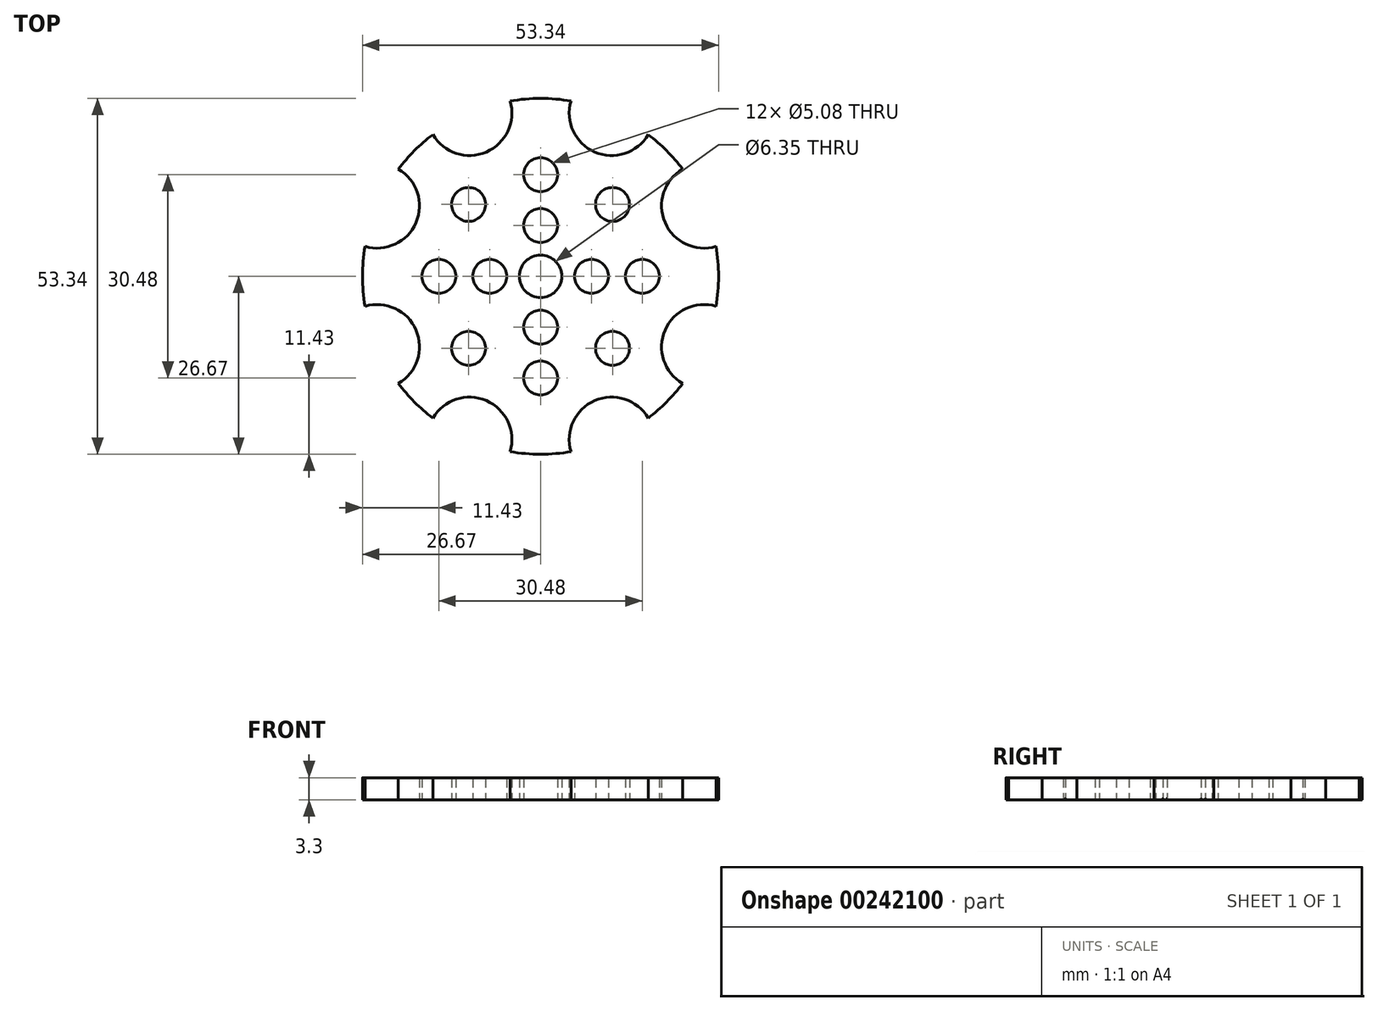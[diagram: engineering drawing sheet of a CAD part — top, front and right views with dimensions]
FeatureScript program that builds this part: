
annotation { "Feature Type Name" : "Feature", "Feature Type Description" : "" }
export const myFeature = defineFeature(function(context is Context, id is Id, definition is map)
    precondition{}
    {
        {
            var Q0;
            Q0=qCreatedBy(makeId("Top.planeOp"),FACE);
            var sketch = newSketch(context, id + "F0", { "sketchPlane" : qUnion([Q0])});
            skCircle(sketch, "E0", {"center": v(0, 0) * mm, "radius": 26.67 * mm});
            skCircle(sketch, "E1", {"center": v(0, 7.62) * mm, "radius": 2.54 * mm});
            skCircle(sketch, "E2", {"center": v(0, 15.24) * mm, "radius": 2.54 * mm});
            skCircle(sketch, "E3", {"center": v(7.62, 0) * mm, "radius": 2.54 * mm});
            skCircle(sketch, "E4", {"center": v(15.24, 0) * mm, "radius": 2.54 * mm});
            skCircle(sketch, "E5.MirrorC", {"center": v(-10.78, -10.78) * mm, "radius": 2.54 * mm});
            skCircle(sketch, "E6.MirrorC", {"center": v(10.78, 10.78) * mm, "radius": 2.54 * mm});
            skCircle(sketch, "E7", {"center": v(-24.48, 10.57) * mm, "radius": 6.35 * mm});
            skCircle(sketch, "E8", {"center": v(-10.65, 24.45) * mm, "radius": 6.35 * mm});
            skCircle(sketch, "E9", {"center": v(0, 0) * mm, "radius": 3.18 * mm});
            skCircle(sketch, "E10.MirrorC", {"center": v(10.65, 24.45) * mm, "radius": 6.35 * mm});
            skCircle(sketch, "E11.MirrorC", {"center": v(24.48, 10.57) * mm, "radius": 6.35 * mm});
            skCircle(sketch, "E12.MirrorC", {"center": v(-24.48, -10.57) * mm, "radius": 6.35 * mm});
            skCircle(sketch, "E13.MirrorC", {"center": v(-10.65, -24.45) * mm, "radius": 6.35 * mm});
            skCircle(sketch, "E14.MirrorC", {"center": v(10.65, -24.45) * mm, "radius": 6.35 * mm});
            skCircle(sketch, "E15.MirrorC", {"center": v(24.48, -10.57) * mm, "radius": 6.35 * mm});
            skCircle(sketch, "E16.MirrorC", {"center": v(0, -7.62) * mm, "radius": 2.54 * mm});
            skCircle(sketch, "E17.MirrorC", {"center": v(0, -15.24) * mm, "radius": 2.54 * mm});
            skCircle(sketch, "E18.MirrorC", {"center": v(10.78, -10.78) * mm, "radius": 2.54 * mm});
            skCircle(sketch, "E19.MirrorC", {"center": v(-10.78, 10.78) * mm, "radius": 2.54 * mm});
            skCircle(sketch, "E20.MirrorC", {"center": v(-7.62, 0) * mm, "radius": 2.54 * mm});
            skCircle(sketch, "E21.MirrorC", {"center": v(-15.24, 0) * mm, "radius": 2.54 * mm});
            skSolve(sketch);
        }
        {
            var Q0;
            Q0=makeQuery(id+"F0.imprint","IMPRINT",FACE,{"disambiguationData":[TD([[makeQuery(id+"F0.imprint","IMPRINT",EDGE,{"derivedFrom":sQuery(id+"F0.wireOp",EDGE,"E1")}),-1.0]])]});
            extrude(context, id + "F1", {"entities" : qUnion([Q0]), "depth" : 3.3 * mm});
        }
        {
            var Q0;
            Q0=makeQuery(id+"F1.opExtrude","CAP_EDGE",EDGE,{"disambiguationData":[OSD([sQuery(id+"F0.wireOp",EDGE,"E21.MirrorC")])],"isStart":true});
            var Q1;
            Q1=makeQuery(id+"F1.opExtrude","CAP_EDGE",EDGE,{"disambiguationData":[OSD([sQuery(id+"F0.wireOp",EDGE,"E19.MirrorC")])],"isStart":true});
            var Q2;
            Q2=makeQuery(id+"F1.opExtrude","CAP_EDGE",EDGE,{"disambiguationData":[OSD([sQuery(id+"F0.wireOp",EDGE,"E20.MirrorC")])],"isStart":true});
            var Q3;
            Q3=makeQuery(id+"F1.opExtrude","CAP_EDGE",EDGE,{"disambiguationData":[OSD([sQuery(id+"F0.wireOp",EDGE,"E5.MirrorC")])],"isStart":true});
            var Q4;
            Q4=makeQuery(id+"F1.opExtrude","CAP_EDGE",EDGE,{"disambiguationData":[OSD([sQuery(id+"F0.wireOp",EDGE,"E16.MirrorC")])],"isStart":true});
            var Q5;
            Q5=makeQuery(id+"F1.opExtrude","CAP_EDGE",EDGE,{"disambiguationData":[OSD([sQuery(id+"F0.wireOp",EDGE,"E17.MirrorC")])],"isStart":true});
            var Q6;
            Q6=makeQuery(id+"F1.opExtrude","CAP_EDGE",EDGE,{"disambiguationData":[OSD([sQuery(id+"F0.wireOp",EDGE,"E18.MirrorC")])],"isStart":true});
            var Q7;
            Q7=makeQuery(id+"F1.opExtrude","CAP_EDGE",EDGE,{"disambiguationData":[OSD([sQuery(id+"F0.wireOp",EDGE,"E3")])],"isStart":true});
            var Q8;
            Q8=makeQuery(id+"F1.opExtrude","CAP_EDGE",EDGE,{"disambiguationData":[OSD([sQuery(id+"F0.wireOp",EDGE,"E1")])],"isStart":true});
            var Q9;
            Q9=makeQuery(id+"F1.opExtrude","CAP_EDGE",EDGE,{"disambiguationData":[OSD([sQuery(id+"F0.wireOp",EDGE,"E9")])],"isStart":true});
            var Q10;
            Q10=makeQuery(id+"F1.opExtrude","CAP_EDGE",EDGE,{"disambiguationData":[OSD([sQuery(id+"F0.wireOp",EDGE,"E6.MirrorC")])],"isStart":true});
            var Q11;
            Q11=makeQuery(id+"F1.opExtrude","CAP_EDGE",EDGE,{"disambiguationData":[OSD([sQuery(id+"F0.wireOp",EDGE,"E2")])],"isStart":true});
            var Q12;
            Q12=makeQuery(id+"F1.opExtrude","CAP_EDGE",EDGE,{"disambiguationData":[OSD([sQuery(id+"F0.wireOp",EDGE,"E4")])],"isStart":true});
            fillet(context, id + "F2", {"entities" : qUnion([Q0, Q1, Q2, Q3, Q4, Q5, Q6, Q7, Q8, Q9, Q10, Q11, Q12]), "radius" : 0.25 * mm, "tangentPropagation" : true, "allowEdgeOverflow" : false});
        }
    });
